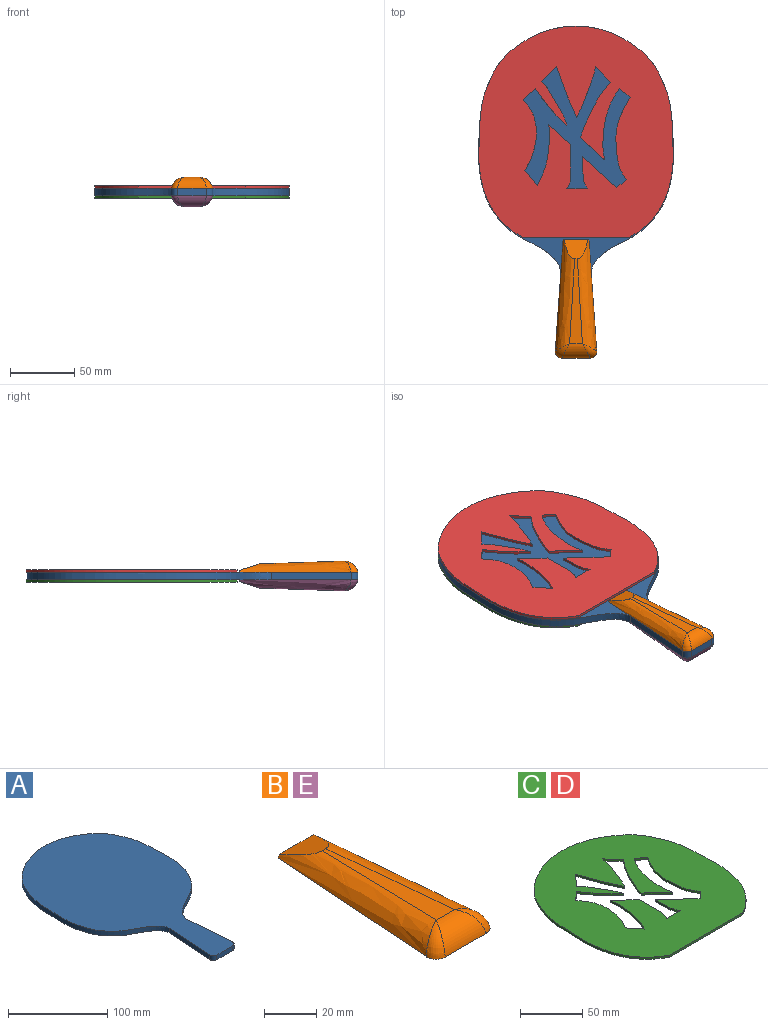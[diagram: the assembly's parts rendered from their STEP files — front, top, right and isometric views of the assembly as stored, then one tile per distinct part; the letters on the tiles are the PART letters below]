
ASSEMBLY  parts=5 mates=4
PART A: 9 faces, bbox 151.6x257x5.8 mm
  f0: plane 61.65x5.8mm, normal (1,0.07,0), area 358.4mm2, adj f1,f5,f6,f8
  f1: extruded ~190x75.64mm, area 1509.4mm2, adj f0,f2,f5,f6
  f2: extruded ~190x75.64mm, area 1509.4mm2, adj f1,f3,f5,f6
  f3: plane 61.65x5.8mm, normal (-1,0.07,0), area 358.4mm2, adj f2,f5,f6,f7
  f4: plane 22.27x5.8mm, normal (0,-1,0), area 129.2mm2, adj f5,f6,f7,f8
  f5: plane 257x151.59mm, normal (0,0,1), area 24161.2mm2, adj f0,f1,f2,f3,f4,f7,f8
  f6: plane 257x151.59mm, normal (0,0,-1), area 24161.2mm2, adj f0,f1,f2,f3,f4,f7,f8
  f7: cylinder r=5mm len=5.8mm, axis (0,0,-1), area 47.6mm2, adj f3,f4,f5,f6
  f8: cylinder r=5mm len=5.8mm, axis (0,0,1), area 47.6mm2, adj f0,f4,f5,f6
PART B: 9 faces, bbox 38.2x159x10.4 mm
  f0: plane 20.02x1.41mm, normal (0,1,0), area 26.6mm2, adj f2,f3,f6,f8
  f1: plane 65.95x9.99mm, normal (0,0.03,1), area 390.1mm2, adj f3,f5,f6,f8
  f2: plane 92x32.29mm, normal (0,0,-1), area 2425.4mm2, adj f0,f3,f4,f5,f6,f7
  f3: bspline ~159.01x20.32mm, area 1042.2mm2, adj f0,f1,f2,f4,f8
  f4: bspline ~11.19x11.14mm, area 52.4mm2, adj f2,f3,f5
  f5: cylinder r=11mm len=22.27mm, axis (1,0,0), area 247.1mm2, adj f1,f2,f4,f7
  f6: bspline ~159.01x20.32mm, area 1042.2mm2, adj f0,f1,f2,f7,f8
  f7: bspline ~11.19x11.14mm, area 53.3mm2, adj f2,f5,f6
  f8: plane 18.27x14.99mm, normal (0,0.32,0.95), area 217.3mm2, adj f0,f1,f3,f6
PART C: 28 faces, bbox 151.6x165x2 mm
  f0: plane 165x151.59mm, normal (0,0,1), area 17674.7mm2, adj f2,f3,f4,f5,f6,f7,f8,f9
  f1: plane 165x151.59mm, normal (0,0,-1), area 17674.7mm2, adj f2,f3,f4,f5,f6,f7,f8,f9
  f2: extruded ~164x75.63mm, area 438.4mm2, adj f0,f1,f3,f4
  f3: plane 83.7x2mm, normal (0,-1,0), area 167.4mm2, adj f0,f1,f2,f4
  f4: extruded ~164x75.63mm, area 438.4mm2, adj f0,f1,f2,f3
  f5: extruded ~34.05x19.51mm, area 79mm2, adj f0,f1,f6,f27
  f6: plane 11.72x11.54mm, normal (0.71,-0.7,0), area 32.9mm2, adj f0,f1,f5,f7
  f7: extruded ~39.72x15.81mm, area 85.6mm2, adj f0,f1,f6,f8
  f8: extruded ~39.72x14.65mm, area 84.9mm2, adj f0,f1,f7,f9
  f9: extruded ~12.47x11.17mm, area 33.5mm2, adj f0,f1,f8,f10
  f10: extruded ~43x22.96mm, area 98.2mm2, adj f0,f1,f9,f11
  f11: extruded ~18.92x17.34mm, area 51.3mm2, adj f0,f1,f10,f12
  f12: extruded ~55.52x13.02mm, area 116.8mm2, adj f0,f1,f11,f13
  f13: plane 8.14x6.95mm, normal (-0.65,-0.76,0), area 21.4mm2, adj f0,f1,f12,f14
  f14: extruded ~63.68x11.09mm, area 135.6mm2, adj f0,f1,f13,f15
  f15: plane 7.53x6.49mm, normal (-0.65,0.76,0), area 19.9mm2, adj f0,f1,f14,f16
  f16: plane 26.78x24.33mm, normal (0.67,0.74,0), area 72.4mm2, adj f0,f1,f15,f17
  f17: plane 16.1x2mm, normal (-1,-0.04,0), area 32.2mm2, adj f0,f1,f16,f18
  f18: extruded ~8.97x3.3mm, area 19.4mm2, adj f0,f1,f17,f19
  f19: plane 16.05x2mm, normal (0,1,0), area 32.1mm2, adj f0,f1,f18,f20
  f20: extruded ~8.97x3.13mm, area 19.4mm2, adj f0,f1,f19,f21
  f21: plane 25.28x2mm, normal (1,0,0), area 50.6mm2, adj f0,f1,f20,f22
  f22: plane 17.18x15.74mm, normal (0.68,0.74,0), area 46.6mm2, adj f0,f1,f21,f23
  f23: extruded ~47.76x9.49mm, area 98.7mm2, adj f0,f1,f22,f24
  f24: plane 11.99x9.82mm, normal (0.77,0.63,0), area 31mm2, adj f0,f1,f23,f25
  f25: extruded ~55.29x10.51mm, area 119.6mm2, adj f0,f1,f24,f26
  f26: plane 9.32x8.34mm, normal (0.67,-0.75,0), area 25mm2, adj f0,f1,f25,f27
  f27: extruded ~28.47x24.63mm, area 75.5mm2, adj f0,f1,f5,f26
PART D: same geometry as C
PART E: same geometry as B
PLACE A t=(-0.16,-4.4,-2.73)mm fixed
PLACE B t=(-0.16,-4.4,-2.73)mm
PLACE C t=(-0.15,-3.52,-10.53)mm
PLACE D t=(-0.15,-3.52,-2.73)mm
PLACE E rot(axis=(0,1,0),180deg) t=(-0.16,-4.4,3.07)mm
MATE slider B.f2 <-> A.f5  axis (0,0,-1) through (-0.16,-128.48,3.07)mm
MATE slider A.f5 <-> D.f1  axis (0,0,1) through (-0.16,27.44,3.07)mm
MATE slider E.f2 <-> A.f6  axis (0,0,1) through (-0.16,-128.48,-2.73)mm
MATE slider C.f0 <-> A.f6  axis (0,0,1) through (-0.16,42.44,-2.73)mm
